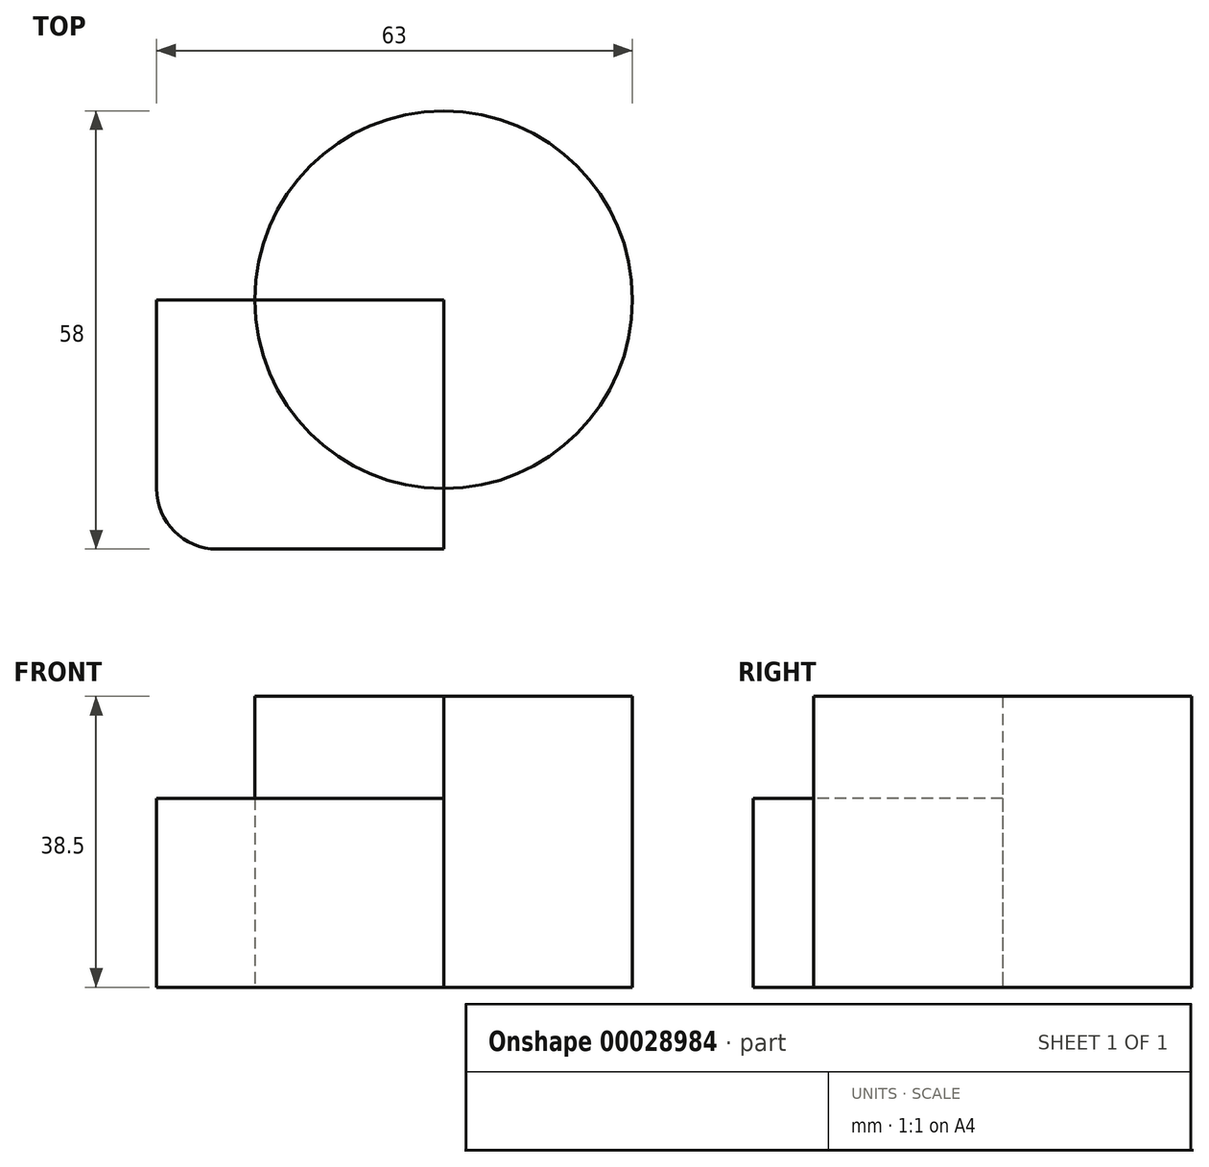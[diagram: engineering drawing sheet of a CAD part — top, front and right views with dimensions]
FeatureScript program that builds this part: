
annotation { "Feature Type Name" : "Feature", "Feature Type Description" : "" }
export const myFeature = defineFeature(function(context is Context, id is Id, definition is map)
    precondition{}
    {
        {
            var Q0;
            Q0=qCreatedBy(makeId("Top.planeOp"),FACE);
            var sketch = newSketch(context, id + "F0", { "sketchPlane" : qUnion([Q0])});
            skLineSegment(sketch, "E0.bottom", {"start": v(-56.84, 4.39) * mm, "end": v(-18.84, 4.39) * mm});
            skLineSegment(sketch, "E0.top", {"start": v(-48.84, -28.61) * mm, "end": v(-18.84, -28.61) * mm});
            skLineSegment(sketch, "E0.left", {"start": v(-56.84, 4.39) * mm, "end": v(-56.84, -20.61) * mm});
            skLineSegment(sketch, "E0.right", {"start": v(-18.84, 4.39) * mm, "end": v(-18.84, -28.61) * mm});
            skCircle(sketch, "E1", {"center": v(-18.84, 4.39) * mm, "radius": 25 * mm});
            skPoint(sketch, "E2.visualSharp", {"position": v(-56.84, -28.61) * mm});
            skArc(sketch, "E2.filletArc", {"start": v(-56.84, -20.61) * mm, "mid": v(-54.5, -26.27) * mm, "end": v(-48.84, -28.61) * mm});
            skSolve(sketch);
        }
        {
            var Q0;
            {var subQ5=sQuery(id+"F0.wireOp",EDGE,"E0.top");Q0=makeQuery(id+"F0.imprint","IMPRINT",FACE,{"disambiguationData":[TD([[makeQuery(id+"F0.imprint","IMPRINT",EDGE,{"derivedFrom":subQ5}),1.0]])]});}
            extrude(context, id + "F1", {"entities" : qUnion([Q0]), "depth" : 25 * mm});
        }
        {
            var Q0;
            Q0=sQuery(id+"F0.wireOp",VERTEX,"E1.center");
            var Q1;
            Q1=makeQuery(id+"F1.opExtrude","SWEPT_BODY",BODY,{"disambiguationData":[OSD([sQuery(id+"F0.wireOp",EDGE,"E0.bottom"),sQuery(id+"F0.wireOp",EDGE,"E0.top"),sQuery(id+"F0.wireOp",EDGE,"E0.left"),sQuery(id+"F0.wireOp",EDGE,"E0.right"),sQuery(id+"F0.wireOp",EDGE,"E1"),sQuery(id+"F0.wireOp",EDGE,"E2.filletArc")])]});
            hole(context, id + "F2", {"style" : HoleStyle.SIMPLE, "holeDiameter" : 5 * mm, "endStyle" : HoleEndStyle.THROUGH, "locations" : qUnion([Q0]), "scope" : qUnion([Q1])});
        }
        {
            var Q0;
            {var subQ0=sQuery(id+"F0.wireOp",EDGE,"E0.right");var subQ1=sQuery(id+"F0.wireOp",EDGE,"E0.bottom");var subQ2=makeQuery(id+"F0.imprint","INTERSECT",VERTEX,{"derivedFrom":[subQ1,subQ0]});Q0=makeQuery(id+"F0.imprint","IMPRINT",FACE,{"disambiguationData":[TD([[makeQuery(id+"F0.imprint","IMPRINT",EDGE,{"disambiguationData":[TD([[subQ2,1.0]])],"derivedFrom":subQ1}),1.0]])]});}
            extrude(context, id + "F3", {"entities" : qUnion([Q0]), "depth" : 38.5 * mm});
        }
    });
